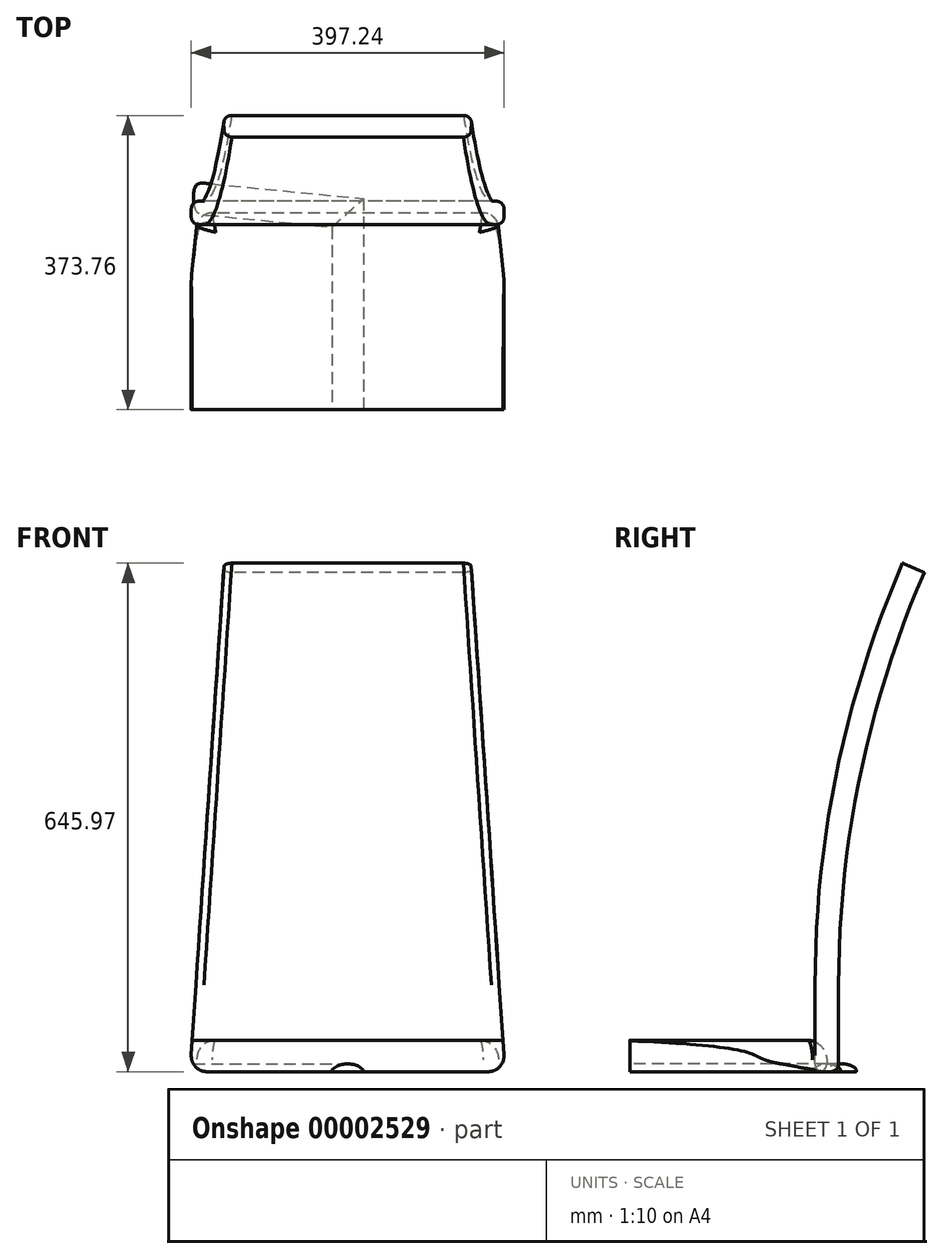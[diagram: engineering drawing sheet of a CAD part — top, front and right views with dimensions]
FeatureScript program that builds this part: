
annotation { "Feature Type Name" : "Feature", "Feature Type Description" : "" }
export const myFeature = defineFeature(function(context is Context, id is Id, definition is map)
    precondition{}
    {
        {
            var Q0;
            Q0=qCreatedBy(makeId("Right.planeOp"),FACE);
            var sketch = newSketch(context, id + "F0", { "sketchPlane" : qUnion([Q0])});
            skLineSegment(sketch, "E0.bottom", {"start": v(0, 0) * mm, "end": v(-415, 0) * mm});
            skLineSegment(sketch, "E0.top", {"start": v(0, 375) * mm, "end": v(-415, 375) * mm, "construction": true});
            skLineSegment(sketch, "E0.left", {"start": v(0, 0) * mm, "end": v(0, 375) * mm, "construction": true});
            skLineSegment(sketch, "E0.right", {"start": v(-415, 0) * mm, "end": v(-415, 375) * mm, "construction": true});
            skFitSpline(sketch, "E1", {"points": [v(-415, 0) * mm, v(0, 375) * mm], "startDerivative": vector(0, 562.5) * mm, "endDerivative": vector(622.5, 0) * mm});
            skSolve(sketch);
        }
        {
            var Q0;
            Q0=qCreatedBy(makeId("Front.planeOp"),FACE);
            var sketch = newSketch(context, id + "F1", { "sketchPlane" : qUnion([Q0])});
            skLineSegment(sketch, "E2.rect.bottom", {"start": v(-20, 10) * mm, "end": v(20, 10) * mm, "construction": true});
            skLineSegment(sketch, "E2.rect.top", {"start": v(-20, -10) * mm, "end": v(20, -10) * mm, "construction": true});
            skLineSegment(sketch, "E2.rect.left", {"start": v(-20, 10) * mm, "end": v(-20, -10) * mm, "construction": true});
            skLineSegment(sketch, "E2.rect.right", {"start": v(20, 10) * mm, "end": v(20, -10) * mm, "construction": true});
            skPoint(sketch, "E2.rect.middle", {"position": v(0, 0) * mm});
            skFitSpline(sketch, "E3", {"points": [v(20, 0) * mm, v(0, 10) * mm, v(-20, 0) * mm, v(0, -10) * mm, v(20, 0) * mm]});
            skSolve(sketch);
        }
        {
            var Q0;
            Q0=qCreatedBy(makeId("Top.planeOp"),FACE);
            var sketch = newSketch(context, id + "F2", { "sketchPlane" : qUnion([Q0])});
            skLineSegment(sketch, "E4", {"start": v(0, 0) * mm, "end": v(-308.56, 29.88) * mm});
            skLineSegment(sketch, "E5", {"start": v(-308.56, 29.88) * mm, "end": v(-388.18, -377.4) * mm});
            skLineSegment(sketch, "E6", {"start": v(-154.28, 14.94) * mm, "end": v(-194.1, -396.2) * mm, "construction": true});
            skLineSegment(sketch, "E7.0", {"start": v(0, 0) * mm, "end": v(0, -415) * mm});
            skLineSegment(sketch, "E8", {"start": v(-388.18, -377.4) * mm, "end": v(0, -415) * mm, "construction": true});
            skSolve(sketch);
        }
        {
            var Q0;
            Q0=sQuery(id+"F2.wireOp",EDGE,"E5");
            cPlane(context, id + "F3", {"entities" : qUnion([Q0]), "cplaneType" : CPlaneType.LINE_ANGLE, "offset" : 150 * mm, "angle" : 90 * degree, "width" : 150 * mm, "height" : 150 * mm});
        }
        {
            var Q0;
            Q0=qCreatedBy(id+"F3.planeOp",FACE);
            var sketch = newSketch(context, id + "F4", { "sketchPlane" : qUnion([Q0])});
            skLineSegment(sketch, "E9.0", {"start": v(-29.88, 0) * mm, "end": v(-444.88, 0) * mm});
            skLineSegment(sketch, "E10.top", {"start": v(-29.88, 375) * mm, "end": v(-444.88, 375) * mm, "construction": true});
            skLineSegment(sketch, "E10.left", {"start": v(-29.88, 0) * mm, "end": v(-29.88, 375) * mm, "construction": true});
            skLineSegment(sketch, "E10.right", {"start": v(-444.88, 0) * mm, "end": v(-444.88, 375) * mm, "construction": true});
            skFitSpline(sketch, "E11", {"points": [v(-29.88, 375) * mm, v(-444.88, 0) * mm], "startDerivative": vector(-622.5, 0) * mm, "endDerivative": vector(0, -562.5) * mm});
            skSolve(sketch);
        }
        {
            var Q0;
            Q0=sQuery(id+"F2.wireOp",EDGE,"E4");
            cPlane(context, id + "F5", {"entities" : qUnion([Q0]), "cplaneType" : CPlaneType.LINE_ANGLE, "offset" : 150 * mm, "angle" : 0 * degree, "width" : 150 * mm, "height" : 150 * mm});
        }
        {
            var Q0;
            Q0=qCreatedBy(id+"F5.planeOp",FACE);
            var sketch = newSketch(context, id + "F6", { "sketchPlane" : qUnion([Q0])});
            skFitSpline(sketch, "E12.0", {"points": [v(-40, 0) * mm, v(-40, 187.5) * mm, v(-20, 375) * mm, v(0, 375) * mm], "construction": true});
            skFitSpline(sketch, "E12.1", {"points": [v(-390, 375) * mm, v(-370, 375) * mm, v(-350, 187.5) * mm, v(-350, 0) * mm], "construction": true});
            skLineSegment(sketch, "E13", {"start": v(0, 375) * mm, "end": v(-310, 375) * mm});
            skSolve(sketch);
        }
        {
            var Q0;
            Q0=makeQuery(id+"F1.imprint","IMPRINT",FACE,{"disambiguationData":[TD([[makeQuery(id+"F1.imprint","IMPRINT",EDGE,{"derivedFrom":sQuery(id+"F1.wireOp",EDGE,"E3")}),1.0]])]});
            var Q1;
            Q1=sQuery(id+"F2.wireOp",EDGE,"E7.0");
            var Q2;
            Q2=sQuery(id+"F0.wireOp",EDGE,"E1");
            var Q3;
            Q3=sQuery(id+"F6.wireOp",EDGE,"E13");
            var Q4;
            Q4=sQuery(id+"F4.wireOp",EDGE,"E11");
            var Q5;
            Q5=sQuery(id+"F2.wireOp",EDGE,"E5");
            var Q6;
            Q6=sQuery(id+"F2.wireOp",EDGE,"E4");
            sweep(context, id + "F7", {"profiles" : qUnion([Q0]), "path" : qUnion([Q1, Q2, Q3, Q4, Q5, Q6])});
        }
        {
            var Q0;
            Q0=qCreatedBy(makeId("Top.planeOp"),FACE);
            var sketch = newSketch(context, id + "F8", { "sketchPlane" : qUnion([Q0])});
            skLineSegment(sketch, "E14", {"start": v(171.93, 0) * mm, "end": v(-171.93, 0) * mm});
            skLineSegment(sketch, "E15", {"start": v(0, 0) * mm, "end": v(0, -430) * mm, "construction": true});
            skArc(sketch, "E16", {"start": v(-214.3, -397.96) * mm, "mid": v(0, -430) * mm, "end": v(214.3, -397.96) * mm});
            skLineSegment(sketch, "E17", {"start": v(228.36, -376.81) * mm, "end": v(191.83, -17.97) * mm});
            skLineSegment(sketch, "E18", {"start": v(-228.36, -376.81) * mm, "end": v(-191.83, -17.97) * mm});
            skLineSegment(sketch, "E19", {"start": v(190, 0) * mm, "end": v(213.2, -227.95) * mm, "construction": true});
            skPoint(sketch, "E20.visualSharp", {"position": v(230, -392.97) * mm});
            skArc(sketch, "E20.filletArc", {"start": v(214.3, -397.96) * mm, "mid": v(225.12, -389.9) * mm, "end": v(228.36, -376.81) * mm});
            skPoint(sketch, "E21.visualSharp", {"position": v(-230, -392.97) * mm});
            skArc(sketch, "E21.filletArc", {"start": v(-228.36, -376.81) * mm, "mid": v(-225.12, -389.9) * mm, "end": v(-214.3, -397.96) * mm});
            skPoint(sketch, "E22.visualSharp", {"position": v(-190, 0) * mm});
            skArc(sketch, "E22.filletArc", {"start": v(-171.93, 0) * mm, "mid": v(-185.34, -5.16) * mm, "end": v(-191.83, -17.97) * mm});
            skPoint(sketch, "E23.visualSharp", {"position": v(190, 0) * mm});
            skArc(sketch, "E23.filletArc", {"start": v(191.83, -17.97) * mm, "mid": v(185.34, -5.16) * mm, "end": v(171.93, 0) * mm});
            skSolve(sketch);
        }
        {
            var Q0;
            Q0=makeQuery(id+"F8.imprint","IMPRINT",FACE,{"disambiguationData":[TD([[makeQuery(id+"F8.imprint","IMPRINT",EDGE,{"derivedFrom":sQuery(id+"F8.wireOp",EDGE,"E14")}),1.0]])]});
            extrude(context, id + "F9", {"entities" : qUnion([Q0]), "depth" : 40 * mm});
        }
        {
            var Q0;
            Q0=makeQuery(id+"F9.opExtrude","CAP_FACE",FACE,{"disambiguationData":[OSD([sQuery(id+"F8.wireOp",EDGE,"E14"),sQuery(id+"F8.wireOp",EDGE,"E16"),sQuery(id+"F8.wireOp",EDGE,"E17"),sQuery(id+"F8.wireOp",EDGE,"E18"),sQuery(id+"F8.wireOp",EDGE,"E20.filletArc"),sQuery(id+"F8.wireOp",EDGE,"E21.filletArc"),sQuery(id+"F8.wireOp",EDGE,"E22.filletArc"),sQuery(id+"F8.wireOp",EDGE,"E23.filletArc")])],"isStart":false});
            fillet(context, id + "F10", {"entities" : qUnion([Q0]), "radius" : 25 * mm, "tangentPropagation" : true, "allowEdgeOverflow" : false});
        }
        {
            var Q0;
            Q0=makeQuery(id+"F9.opExtrude","CAP_FACE",FACE,{"disambiguationData":[OSD([sQuery(id+"F8.wireOp",EDGE,"E14"),sQuery(id+"F8.wireOp",EDGE,"E16"),sQuery(id+"F8.wireOp",EDGE,"E17"),sQuery(id+"F8.wireOp",EDGE,"E18"),sQuery(id+"F8.wireOp",EDGE,"E20.filletArc"),sQuery(id+"F8.wireOp",EDGE,"E21.filletArc"),sQuery(id+"F8.wireOp",EDGE,"E22.filletArc"),sQuery(id+"F8.wireOp",EDGE,"E23.filletArc")])],"isStart":true});
            fillet(context, id + "F11", {"entities" : qUnion([Q0]), "radius" : 10 * mm, "tangentPropagation" : true, "allowEdgeOverflow" : false});
        }
        {
            var Q0;
            Q0=qCreatedBy(makeId("Right.planeOp"),FACE);
            var sketch = newSketch(context, id + "F12", { "sketchPlane" : qUnion([Q0])});
            skLineSegment(sketch, "E24", {"start": v(0, -110) * mm, "end": v(0, 110) * mm});
            skArc(sketch, "E25", {"start": v(0, 110) * mm, "mid": v(27.79, 380.65) * mm, "end": v(110, 640) * mm});
            skSolve(sketch);
        }
        {
            var Q0;
            Q0=qCreatedBy(makeId("Top.planeOp"),FACE);
            var sketch = newSketch(context, id + "F13", { "sketchPlane" : qUnion([Q0])});
            skLineSegment(sketch, "E26.rect.bottom", {"start": v(200, -15) * mm, "end": v(-200, -15) * mm});
            skLineSegment(sketch, "E26.rect.top", {"start": v(200, 15) * mm, "end": v(-200, 15) * mm});
            skLineSegment(sketch, "E26.rect.left", {"start": v(200, -15) * mm, "end": v(200, 15) * mm});
            skLineSegment(sketch, "E26.rect.right", {"start": v(-200, -15) * mm, "end": v(-200, 15) * mm});
            skPoint(sketch, "E26.rect.middle", {"position": v(0, 0) * mm});
            skSolve(sketch);
        }
        {
            var Q0;
            Q0=makeQuery(id+"F13.imprint","IMPRINT",FACE,{"disambiguationData":[TD([[makeQuery(id+"F13.imprint","IMPRINT",EDGE,{"derivedFrom":sQuery(id+"F13.wireOp",EDGE,"E26.rect.bottom")}),-1.0]])]});
            var Q1;
            Q1=sQuery(id+"F12.wireOp",EDGE,"E24");
            var Q2;
            Q2=sQuery(id+"F12.wireOp",EDGE,"E25");
            sweep(context, id + "F14", {"profiles" : qUnion([Q0]), "path" : qUnion([Q1, Q2])});
        }
        {
            var Q0;
            Q0=qCreatedBy(makeId("Front.planeOp"),FACE);
            var sketch = newSketch(context, id + "F15", { "sketchPlane" : qUnion([Q0])});
            skLineSegment(sketch, "E27", {"start": v(-178.62, 0) * mm, "end": v(178.62, 0) * mm});
            skLineSegment(sketch, "E28", {"start": v(0, 0) * mm, "end": v(0, 690) * mm, "construction": true});
            skLineSegment(sketch, "E29", {"start": v(-156.12, 655.46) * mm, "end": v(-198.57, 21.34) * mm});
            skLineSegment(sketch, "E30", {"start": v(156.12, 655.46) * mm, "end": v(198.57, 21.34) * mm});
            skLineSegment(sketch, "E31", {"start": v(-155.15, 670) * mm, "end": v(155.15, 670) * mm, "construction": true});
            skArc(sketch, "E32", {"start": v(140.77, 673.58) * mm, "mid": v(0, 690) * mm, "end": v(-140.77, 673.58) * mm});
            skPoint(sketch, "E33.orphan", {"position": v(-200, 746.88) * mm});
            skPoint(sketch, "E34.visualSharp", {"position": v(-155.15, 670) * mm});
            skArc(sketch, "E34.filletArc", {"start": v(-140.77, 673.58) * mm, "mid": v(-151.43, 667.05) * mm, "end": v(-156.12, 655.46) * mm});
            skPoint(sketch, "E35.visualSharp", {"position": v(155.15, 670) * mm});
            skArc(sketch, "E35.filletArc", {"start": v(156.12, 655.46) * mm, "mid": v(151.43, 667.05) * mm, "end": v(140.77, 673.58) * mm});
            skPoint(sketch, "E36.visualSharp", {"position": v(-200, 0) * mm});
            skArc(sketch, "E36.filletArc", {"start": v(-198.57, 21.34) * mm, "mid": v(-193.22, 6.34) * mm, "end": v(-178.62, 0) * mm});
            skPoint(sketch, "E37.visualSharp", {"position": v(200, 0) * mm});
            skArc(sketch, "E37.filletArc", {"start": v(178.62, 0) * mm, "mid": v(193.22, 6.34) * mm, "end": v(198.57, 21.34) * mm});
            skSolve(sketch);
        }
        {
            var Q0;
            Q0=makeQuery(id+"F15.imprint","IMPRINT",FACE,{"disambiguationData":[TD([[makeQuery(id+"F15.imprint","IMPRINT",EDGE,{"derivedFrom":sQuery(id+"F15.wireOp",EDGE,"E27")}),1.0]])]});
            extrude(context, id + "F16", {"entities" : qUnion([Q0]), "operationType" : NewBodyOperationType.INTERSECT, "endBound" : BoundingType.SYMMETRIC, "oppositeDirection" : true, "depth" : 500 * mm});
        }
        {
            var Q0;
            Q0=makeQuery(id+"F16.boolean.opBoolean","INTERSECT",EDGE,{"derivedFrom":[makeQuery(id+"F14.opSweep","SWEPT_FACE",FACE,{"disambiguationData":[OSD([sQuery(id+"F12.wireOp",EDGE,"E25"),sQuery(id+"F13.wireOp",EDGE,"E26.rect.bottom")])]}),makeQuery(id+"F16.opExtrude","SWEPT_FACE",FACE,{"disambiguationData":[OSD([sQuery(id+"F15.wireOp",EDGE,"E29")])]})]});
            var Q1;
            Q1=makeQuery(id+"F16.boolean.opBoolean","INTERSECT",EDGE,{"derivedFrom":[makeQuery(id+"F14.opSweep","SWEPT_FACE",FACE,{"disambiguationData":[OSD([sQuery(id+"F12.wireOp",EDGE,"E24"),sQuery(id+"F13.wireOp",EDGE,"E26.rect.bottom")])]}),makeQuery(id+"F16.opExtrude","SWEPT_FACE",FACE,{"disambiguationData":[OSD([sQuery(id+"F15.wireOp",EDGE,"E29")])]})]});
            var Q2;
            Q2=makeQuery(id+"F16.boolean.opBoolean","INTERSECT",EDGE,{"derivedFrom":[makeQuery(id+"F14.opSweep","SWEPT_FACE",FACE,{"disambiguationData":[OSD([sQuery(id+"F12.wireOp",EDGE,"E25"),sQuery(id+"F13.wireOp",EDGE,"E26.rect.top")])]}),makeQuery(id+"F16.opExtrude","SWEPT_FACE",FACE,{"disambiguationData":[OSD([sQuery(id+"F15.wireOp",EDGE,"E29")])]})]});
            var Q3;
            Q3=makeQuery(id+"F16.boolean.opBoolean","INTERSECT",EDGE,{"derivedFrom":[makeQuery(id+"F14.opSweep","SWEPT_FACE",FACE,{"disambiguationData":[OSD([sQuery(id+"F12.wireOp",EDGE,"E24"),sQuery(id+"F13.wireOp",EDGE,"E26.rect.top")])]}),makeQuery(id+"F16.opExtrude","SWEPT_FACE",FACE,{"disambiguationData":[OSD([sQuery(id+"F15.wireOp",EDGE,"E29")])]})]});
            fillet(context, id + "F17", {"entities" : qUnion([Q0, Q1, Q2, Q3]), "radius" : 10 * mm, "tangentPropagation" : true, "allowEdgeOverflow" : false});
        }
    });
